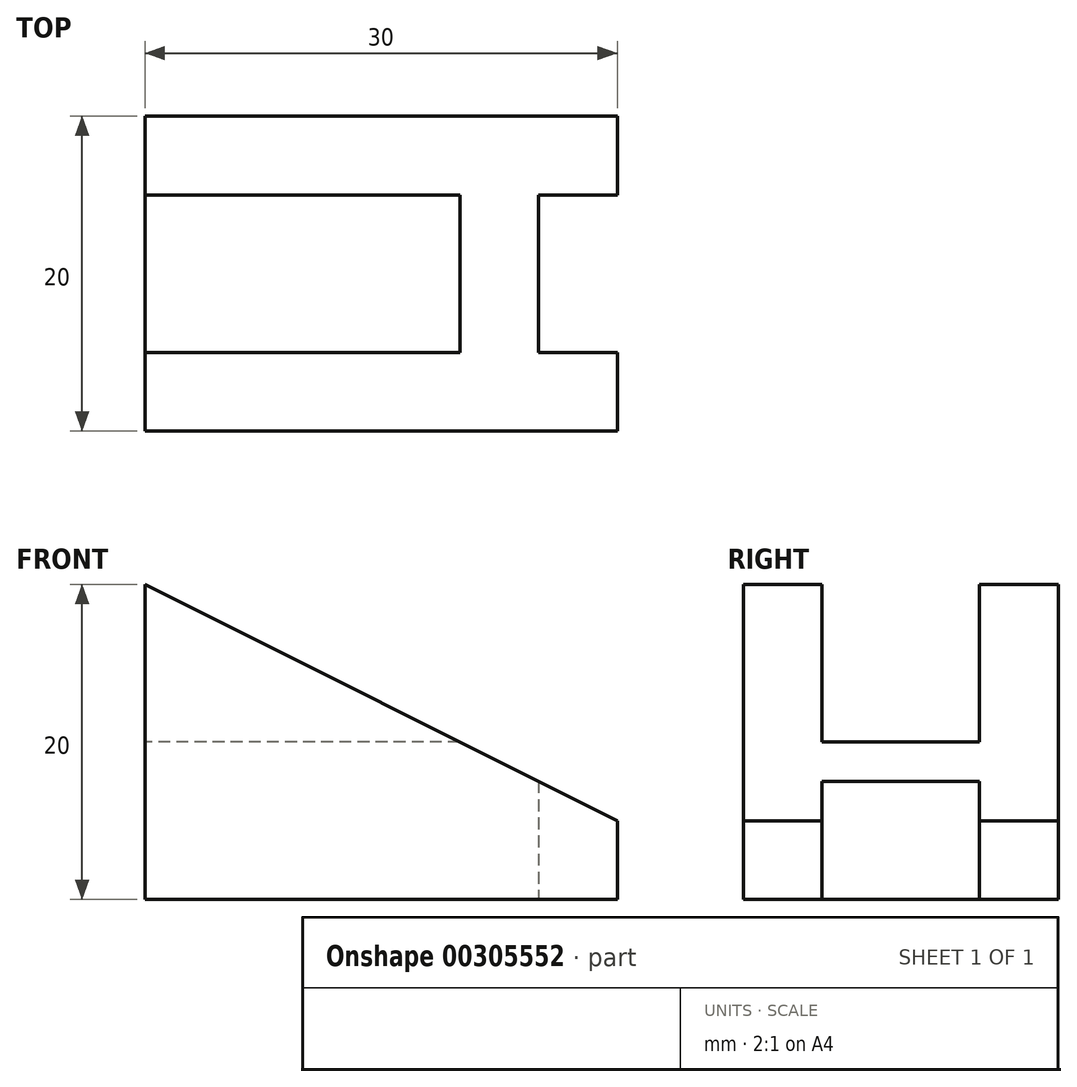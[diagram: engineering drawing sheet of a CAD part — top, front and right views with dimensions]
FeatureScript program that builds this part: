
annotation { "Feature Type Name" : "Feature", "Feature Type Description" : "" }
export const myFeature = defineFeature(function(context is Context, id is Id, definition is map)
    precondition{}
    {
        {
            var Q0;
            Q0=qCreatedBy(makeId("Front.planeOp"),FACE);
            var sketch = newSketch(context, id + "F0", { "sketchPlane" : qUnion([Q0])});
            skLineSegment(sketch, "E0", {"start": v(0, 0) * mm, "end": v(0, 20) * mm});
            skLineSegment(sketch, "E1", {"start": v(0, 20) * mm, "end": v(30, 5) * mm});
            skLineSegment(sketch, "E2", {"start": v(30, 5) * mm, "end": v(30, 0) * mm});
            skLineSegment(sketch, "E3", {"start": v(30, 0) * mm, "end": v(0, 0) * mm});
            skSolve(sketch);
        }
        {
            var Q0;
            Q0 = qSketchRegion(id + "F0", true);
            extrude(context, id + "F1", {"entities" : qUnion([Q0]), "endBound" : BoundingType.SYMMETRIC, "depth" : 20 * mm});
        }
        {
            var Q0;
            Q0=qCreatedBy(makeId("Right.planeOp"),FACE);
            var sketch = newSketch(context, id + "F2", { "sketchPlane" : qUnion([Q0])});
            skLineSegment(sketch, "E4", {"start": v(-5, 20) * mm, "end": v(-5, 10) * mm});
            skLineSegment(sketch, "E5", {"start": v(-5, 10) * mm, "end": v(5, 10) * mm});
            skLineSegment(sketch, "E6", {"start": v(5, 10) * mm, "end": v(5, 20) * mm});
            skLineSegment(sketch, "E7", {"start": v(5, 20) * mm, "end": v(-5, 20) * mm});
            skSolve(sketch);
        }
        {
            var Q0;
            Q0 = qSketchRegion(id + "F2", true);
            extrude(context, id + "F3", {"entities" : qUnion([Q0]), "operationType" : NewBodyOperationType.REMOVE, "endBound" : BoundingType.THROUGH_ALL, "depth" : 25 * mm});
        }
        {
            var Q0;
            Q0=qCreatedBy(makeId("Top.planeOp"),FACE);
            var sketch = newSketch(context, id + "F4", { "sketchPlane" : qUnion([Q0])});
            skLineSegment(sketch, "E8.bottom", {"start": v(30, 5) * mm, "end": v(25, 5) * mm});
            skLineSegment(sketch, "E8.top", {"start": v(30, -5) * mm, "end": v(25, -5) * mm});
            skLineSegment(sketch, "E8.left", {"start": v(30, 5) * mm, "end": v(30, -5) * mm});
            skLineSegment(sketch, "E8.right", {"start": v(25, 5) * mm, "end": v(25, -5) * mm});
            skSolve(sketch);
        }
        {
            var Q0;
            Q0 = qSketchRegion(id + "F4", true);
            extrude(context, id + "F5", {"entities" : qUnion([Q0]), "operationType" : NewBodyOperationType.REMOVE, "endBound" : BoundingType.THROUGH_ALL, "depth" : 25 * mm});
        }
    });
